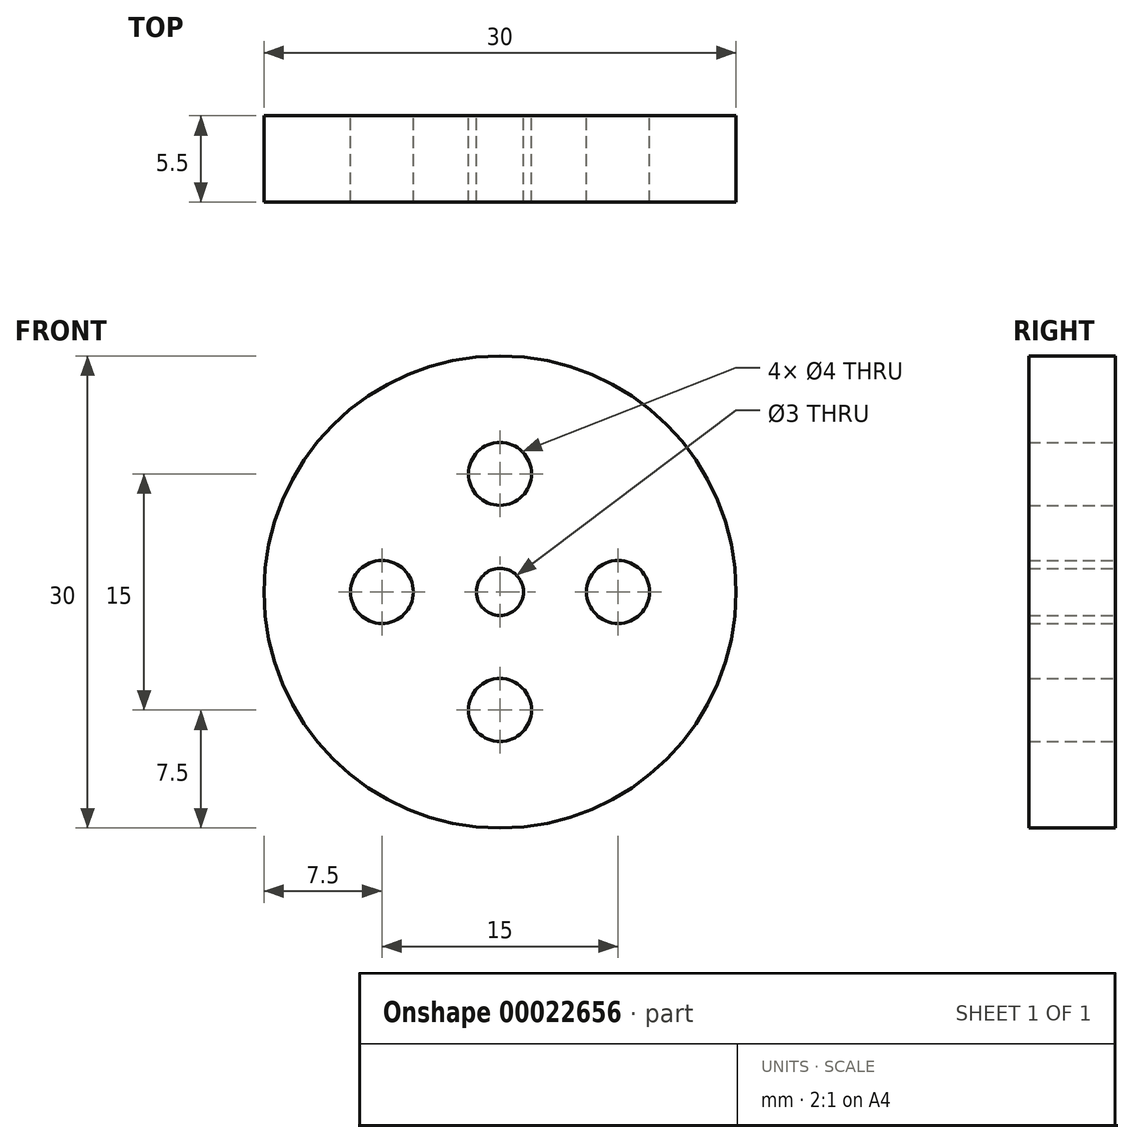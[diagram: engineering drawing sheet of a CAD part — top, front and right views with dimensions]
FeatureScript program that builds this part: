
annotation { "Feature Type Name" : "Feature", "Feature Type Description" : "" }
export const myFeature = defineFeature(function(context is Context, id is Id, definition is map)
    precondition{}
    {
        {
            var Q0;
            Q0=qCreatedBy(makeId("Front.planeOp"),FACE);
            var sketch = newSketch(context, id + "F0", { "sketchPlane" : qUnion([Q0])});
            skCircle(sketch, "E0", {"center": v(0, 0) * mm, "radius": 1.5 * mm});
            skCircle(sketch, "E1", {"center": v(0, 0) * mm, "radius": 4 * mm});
            skCircle(sketch, "E2", {"center": v(0, 0) * mm, "radius": 15 * mm});
            skCircle(sketch, "E3", {"center": v(0, 0) * mm, "radius": 13 * mm});
            skCircle(sketch, "E4", {"center": v(0, 7.5) * mm, "radius": 2 * mm});
            skCircle(sketch, "E5.1.0", {"center": v(-7.5, 0) * mm, "radius": 2 * mm});
            skCircle(sketch, "E5.2.0", {"center": v(0, -7.5) * mm, "radius": 2 * mm});
            skCircle(sketch, "E5.3.0", {"center": v(7.5, 0) * mm, "radius": 2 * mm});
            skSolve(sketch);
        }
        {
            var Q0;
            Q0=makeQuery(id+"F0.imprint","IMPRINT",FACE,{"disambiguationData":[TD([[makeQuery(id+"F0.imprint","IMPRINT",EDGE,{"derivedFrom":sQuery(id+"F0.wireOp",EDGE,"E2")}),1.0]])]});
            var Q1;
            Q1=makeQuery(id+"F0.imprint","IMPRINT",FACE,{"disambiguationData":[TD([[makeQuery(id+"F0.imprint","IMPRINT",EDGE,{"derivedFrom":sQuery(id+"F0.wireOp",EDGE,"E0")}),-1.0]])]});
            var Q2;
            Q2=makeQuery(id+"F0.imprint","IMPRINT",FACE,{"disambiguationData":[TD([[makeQuery(id+"F0.imprint","IMPRINT",EDGE,{"derivedFrom":sQuery(id+"F0.wireOp",EDGE,"E1")}),-1.0]])]});
            extrude(context, id + "F1", {"entities" : qUnion([Q0, Q1, Q2]), "endBound" : BoundingType.SYMMETRIC, "depth" : 5.5 * mm});
        }
    });
